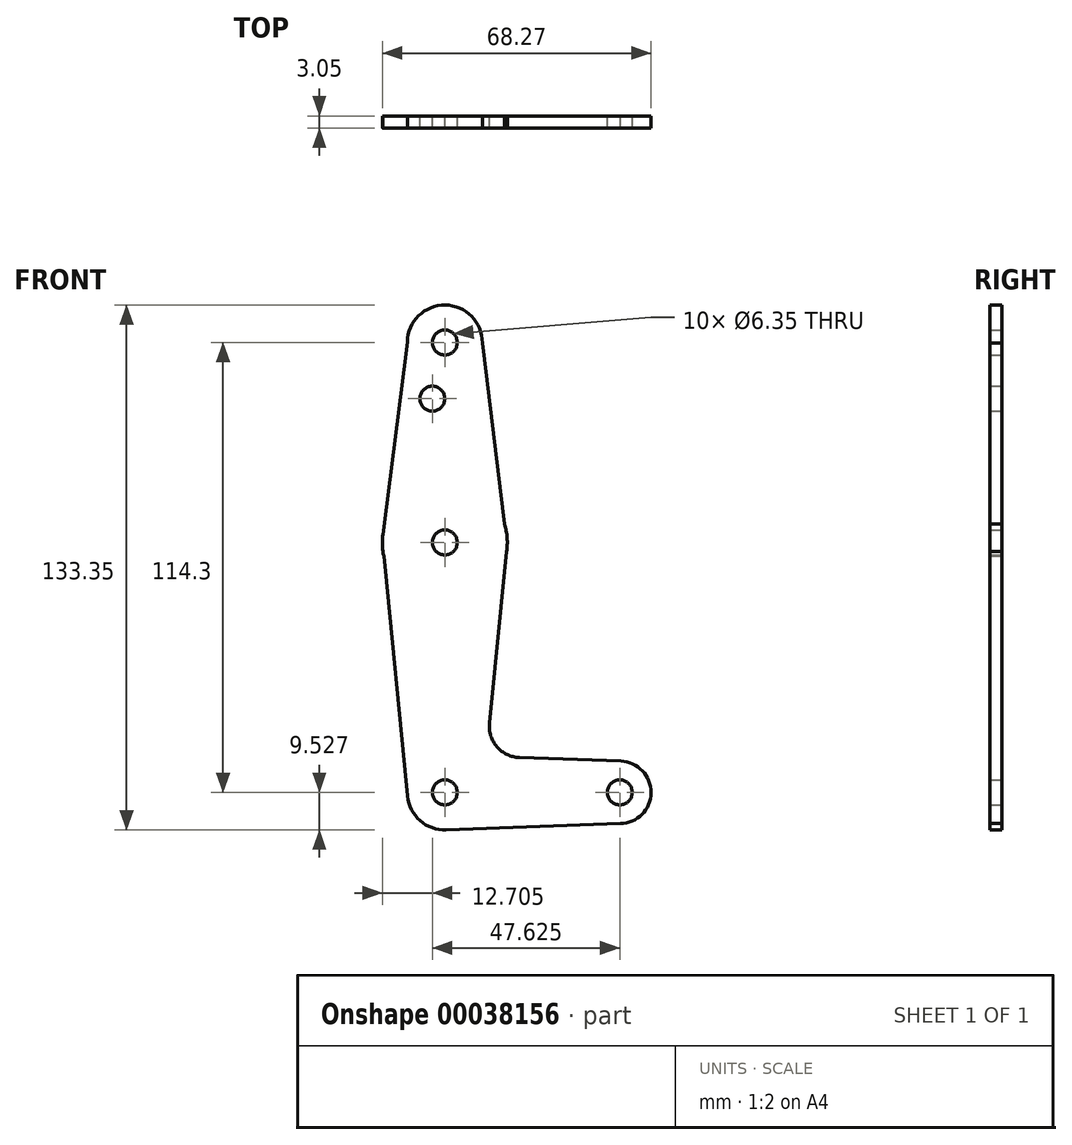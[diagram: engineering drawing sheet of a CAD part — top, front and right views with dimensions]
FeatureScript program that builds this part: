
annotation { "Feature Type Name" : "Feature", "Feature Type Description" : "" }
export const myFeature = defineFeature(function(context is Context, id is Id, definition is map)
    precondition{}
    {
        {
            var Q0;
            Q0=qCreatedBy(makeId("Front.planeOp"),FACE);
            var sketch = newSketch(context, id + "F0", { "sketchPlane" : qUnion([Q0])});
            skLineSegment(sketch, "E0", {"start": v(-22.31, 80.94) * mm, "end": v(-22.31, -33.36) * mm, "construction": true});
            skLineSegment(sketch, "E1", {"start": v(-22.31, -33.36) * mm, "end": v(22.14, -33.36) * mm, "construction": true});
            skCircle(sketch, "E2", {"center": v(-22.31, 80.94) * mm, "radius": 9.53 * mm});
            skCircle(sketch, "E3", {"center": v(-22.31, 30.14) * mm, "radius": 15.88 * mm});
            skCircle(sketch, "E4", {"center": v(-22.31, -33.36) * mm, "radius": 9.53 * mm});
            skCircle(sketch, "E5", {"center": v(22.14, -33.36) * mm, "radius": 7.94 * mm});
            skLineSegment(sketch, "E6", {"start": v(-12.79, 80.86) * mm, "end": v(-6.46, 29.32) * mm});
            skLineSegment(sketch, "E7", {"start": v(-31.83, 81.06) * mm, "end": v(-38.06, 32.14) * mm});
            skLineSegment(sketch, "E8", {"start": v(-38.06, 32.14) * mm, "end": v(-38.18, 30.5) * mm});
            skLineSegment(sketch, "E9", {"start": v(-38.18, 30.5) * mm, "end": v(-31.79, -34.3) * mm});
            skLineSegment(sketch, "E10", {"start": v(-6.46, 29.32) * mm, "end": v(-10.97, -15.77) * mm});
            skLineSegment(sketch, "E11", {"start": v(22.4, -25.43) * mm, "end": v(-3.35, -24.5) * mm});
            skLineSegment(sketch, "E12", {"start": v(22.28, -41.3) * mm, "end": v(-21.97, -42.88) * mm});
            skCircle(sketch, "E13", {"center": v(-22.31, 80.94) * mm, "radius": 3.18 * mm});
            skCircle(sketch, "E14", {"center": v(-22.31, 30.14) * mm, "radius": 3.18 * mm});
            skCircle(sketch, "E15", {"center": v(-22.31, -33.36) * mm, "radius": 3.18 * mm});
            skCircle(sketch, "E16", {"center": v(22.14, -33.36) * mm, "radius": 3.18 * mm});
            skArc(sketch, "E17.filletArc", {"start": v(-10.97, -15.77) * mm, "mid": v(-9.05, -21.8) * mm, "end": v(-3.35, -24.5) * mm});
            skCircle(sketch, "E18", {"center": v(-25.49, 66.66) * mm, "radius": 3.18 * mm});
            skSolve(sketch);
        }
        {
            var Q0;
            Q0 = qSketchRegion(id + "F0", true);
            extrude(context, id + "F1", {"entities" : qUnion([Q0]), "depth" : 3.05 * mm});
        }
    });
